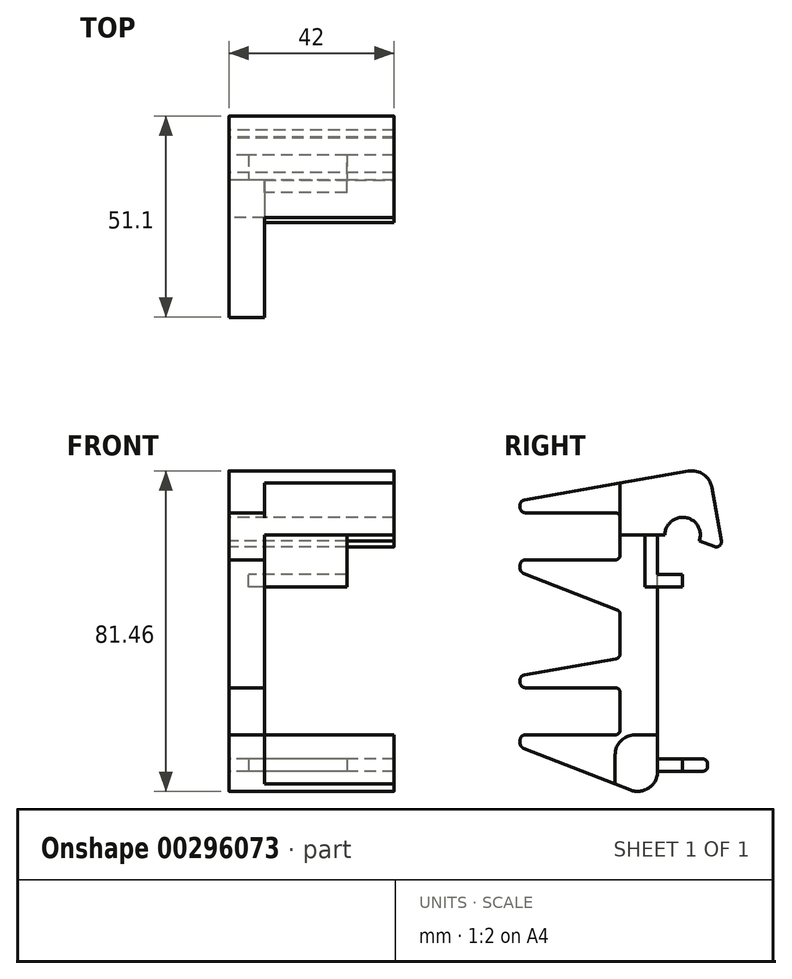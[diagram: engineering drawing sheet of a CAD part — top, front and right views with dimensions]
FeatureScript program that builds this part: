
annotation { "Feature Type Name" : "Feature", "Feature Type Description" : "" }
export const myFeature = defineFeature(function(context is Context, id is Id, definition is map)
    precondition{}
    {
        {
            var Q0;
            Q0=qCreatedBy(makeId("Right.planeOp"),FACE);
            var sketch = newSketch(context, id + "F0", { "sketchPlane" : qUnion([Q0])});
            skLineSegment(sketch, "E0.right", {"start": v(0, 67.5) * mm, "end": v(0, 0) * mm});
            skCircle(sketch, "E1", {"center": v(6.35, 67.5) * mm, "radius": 4.5 * mm});
            skLineSegment(sketch, "E2", {"start": v(1.85, 67.5) * mm, "end": v(0, 67.5) * mm});
            skLineSegment(sketch, "E3", {"start": v(16.55, 63.8) * mm, "end": v(10.58, 65.96) * mm});
            skLineSegment(sketch, "E4", {"start": v(-34.93, 58.1) * mm, "end": v(-34.93, 61.15) * mm});
            skLineSegment(sketch, "E5", {"start": v(-34.92, 61.15) * mm, "end": v(-9.52, 61.15) * mm});
            skLineSegment(sketch, "E6", {"start": v(-9.53, 61.15) * mm, "end": v(-9.53, 73.15) * mm});
            skLineSegment(sketch, "E7", {"start": v(-9.52, 73.15) * mm, "end": v(-34.92, 73.15) * mm});
            skLineSegment(sketch, "E8", {"start": v(-34.93, 73.15) * mm, "end": v(-34.93, 76.2) * mm});
            skLineSegment(sketch, "E9", {"start": v(-34.93, 31.75) * mm, "end": v(-34.93, 28.7) * mm});
            skLineSegment(sketch, "E10", {"start": v(-34.93, 28.7) * mm, "end": v(-9.52, 28.7) * mm});
            skLineSegment(sketch, "E11", {"start": v(-9.52, 28.7) * mm, "end": v(-9.52, 16.7) * mm});
            skLineSegment(sketch, "E12", {"start": v(-9.52, 16.7) * mm, "end": v(-34.92, 16.7) * mm});
            skLineSegment(sketch, "E13", {"start": v(-34.93, 16.7) * mm, "end": v(-34.93, 13.65) * mm});
            skLineSegment(sketch, "E14", {"start": v(-34.92, 13.65) * mm, "end": v(0, 0) * mm});
            skLineSegment(sketch, "E15", {"start": v(-34.92, 58.1) * mm, "end": v(-9.52, 48.17) * mm});
            skLineSegment(sketch, "E16", {"start": v(-9.53, 48.17) * mm, "end": v(-9.53, 36.23) * mm});
            skLineSegment(sketch, "E17", {"start": v(-34.93, 76.2) * mm, "end": v(12.87, 84.63) * mm});
            skLineSegment(sketch, "E18", {"start": v(-34.93, 31.75) * mm, "end": v(-9.52, 36.23) * mm});
            skLineSegment(sketch, "E19", {"start": v(12.87, 84.63) * mm, "end": v(16.55, 63.8) * mm});
            skSolve(sketch);
        }
        {
            var Q0;
            Q0=makeQuery(id+"F0.imprint","IMPRINT",FACE,{"disambiguationData":[TD([[makeQuery(id+"F0.imprint","IMPRINT",EDGE,{"derivedFrom":sQuery(id+"F0.wireOp",EDGE,"E0.right")}),-1.0]])]});
            extrude(context, id + "F1", {"entities" : qUnion([Q0]), "depth" : 42 * mm});
        }
        {
            var Q0;
            Q0=makeQuery(id+"F1.opExtrude","SWEPT_EDGE",EDGE,{"disambiguationData":[OSD([sQuery(id+"F0.wireOp",EDGE,"E17"),sQuery(id+"F0.wireOp",EDGE,"E19")])]});
            var Q1;
            Q1=makeQuery(id+"F1.opExtrude","SWEPT_EDGE",EDGE,{"disambiguationData":[OSD([sQuery(id+"F0.wireOp",EDGE,"E0.right"),sQuery(id+"F0.wireOp",EDGE,"E14")])]});
            fillet(context, id + "F2", {"entities" : qUnion([Q0, Q1]), "radius" : 5.08 * mm, "tangentPropagation" : true, "allowEdgeOverflow" : false});
        }
        {
            var Q0;
            Q0=makeQuery(id+"F1.opExtrude","SWEPT_EDGE",EDGE,{"disambiguationData":[OSD([sQuery(id+"F0.wireOp",EDGE,"E3"),sQuery(id+"F0.wireOp",EDGE,"E19")])]});
            var Q1;
            Q1=makeQuery(id+"F1.opExtrude","SWEPT_EDGE",EDGE,{"disambiguationData":[OSD([sQuery(id+"F0.wireOp",EDGE,"E10"),sQuery(id+"F0.wireOp",EDGE,"E11")])]});
            var Q2;
            Q2=makeQuery(id+"F1.opExtrude","SWEPT_EDGE",EDGE,{"disambiguationData":[OSD([sQuery(id+"F0.wireOp",EDGE,"E15"),sQuery(id+"F0.wireOp",EDGE,"E16")])]});
            var Q3;
            Q3=makeQuery(id+"F1.opExtrude","SWEPT_EDGE",EDGE,{"disambiguationData":[OSD([sQuery(id+"F0.wireOp",EDGE,"E6"),sQuery(id+"F0.wireOp",EDGE,"E7")])]});
            var Q4;
            Q4=makeQuery(id+"F1.opExtrude","SWEPT_EDGE",EDGE,{"disambiguationData":[OSD([sQuery(id+"F0.wireOp",EDGE,"E5"),sQuery(id+"F0.wireOp",EDGE,"E6")])]});
            var Q5;
            Q5=makeQuery(id+"F1.opExtrude","SWEPT_EDGE",EDGE,{"disambiguationData":[OSD([sQuery(id+"F0.wireOp",EDGE,"E11"),sQuery(id+"F0.wireOp",EDGE,"E12")])]});
            var Q6;
            Q6=makeQuery(id+"F1.opExtrude","SWEPT_EDGE",EDGE,{"disambiguationData":[OSD([sQuery(id+"F0.wireOp",EDGE,"E12"),sQuery(id+"F0.wireOp",EDGE,"E13")])]});
            var Q7;
            Q7=makeQuery(id+"F1.opExtrude","SWEPT_EDGE",EDGE,{"disambiguationData":[OSD([sQuery(id+"F0.wireOp",EDGE,"E13"),sQuery(id+"F0.wireOp",EDGE,"E14")])]});
            var Q8;
            Q8=makeQuery(id+"F1.opExtrude","SWEPT_EDGE",EDGE,{"disambiguationData":[OSD([sQuery(id+"F0.wireOp",EDGE,"E9"),sQuery(id+"F0.wireOp",EDGE,"E10")])]});
            var Q9;
            Q9=makeQuery(id+"F1.opExtrude","SWEPT_EDGE",EDGE,{"disambiguationData":[OSD([sQuery(id+"F0.wireOp",EDGE,"E4"),sQuery(id+"F0.wireOp",EDGE,"E5")])]});
            var Q10;
            Q10=makeQuery(id+"F1.opExtrude","SWEPT_EDGE",EDGE,{"disambiguationData":[OSD([sQuery(id+"F0.wireOp",EDGE,"E4"),sQuery(id+"F0.wireOp",EDGE,"E15")])]});
            var Q11;
            Q11=makeQuery(id+"F1.opExtrude","SWEPT_EDGE",EDGE,{"disambiguationData":[OSD([sQuery(id+"F0.wireOp",EDGE,"E9"),sQuery(id+"F0.wireOp",EDGE,"E18")])]});
            var Q12;
            Q12=makeQuery(id+"F1.opExtrude","SWEPT_EDGE",EDGE,{"disambiguationData":[OSD([sQuery(id+"F0.wireOp",EDGE,"E7"),sQuery(id+"F0.wireOp",EDGE,"E8")])]});
            var Q13;
            Q13=makeQuery(id+"F1.opExtrude","SWEPT_EDGE",EDGE,{"disambiguationData":[OSD([sQuery(id+"F0.wireOp",EDGE,"E8"),sQuery(id+"F0.wireOp",EDGE,"E17")])]});
            var Q14;
            Q14=makeQuery(id+"F1.opExtrude","SWEPT_EDGE",EDGE,{"disambiguationData":[OSD([sQuery(id+"F0.wireOp",EDGE,"E16"),sQuery(id+"F0.wireOp",EDGE,"E18")])]});
            fillet(context, id + "F3", {"entities" : qUnion([Q0, Q1, Q2, Q3, Q4, Q5, Q6, Q7, Q8, Q9, Q10, Q11, Q12, Q13, Q14]), "radius" : 1.27 * mm, "tangentPropagation" : true, "allowEdgeOverflow" : false});
        }
        {
            var Q0;
            Q0=makeQuery(id+"F1.opExtrude","SWEPT_FACE",FACE,{"disambiguationData":[OSD([sQuery(id+"F0.wireOp",EDGE,"E0.right")])]});
            var sketch = newSketch(context, id + "F4", { "sketchPlane" : qUnion([Q0])});
            skLineSegment(sketch, "E20.bottom", {"start": v(-30, 10.62) * mm, "end": v(-5, 10.62) * mm});
            skLineSegment(sketch, "E20.top", {"start": v(-30, 7.44) * mm, "end": v(-5, 7.44) * mm});
            skLineSegment(sketch, "E20.left", {"start": v(-30, 10.62) * mm, "end": v(-30, 7.44) * mm});
            skLineSegment(sketch, "E20.right", {"start": v(-5, 10.62) * mm, "end": v(-5, 7.44) * mm});
            skSolve(sketch);
        }
        {
            var Q0;
            Q0 = qSketchRegion(id + "F4", true);
            extrude(context, id + "F5", {"entities" : qUnion([Q0]), "operationType" : NewBodyOperationType.ADD, "depth" : 12.7 * mm});
        }
        {
            var Q0;
            Q0=makeQuery(id+"F1.opExtrude","CAP_FACE",FACE,{"disambiguationData":[OSD([sQuery(id+"F0.wireOp",EDGE,"E0.right"),sQuery(id+"F0.wireOp",EDGE,"E1"),sQuery(id+"F0.wireOp",EDGE,"E2"),sQuery(id+"F0.wireOp",EDGE,"E3"),sQuery(id+"F0.wireOp",EDGE,"E4"),sQuery(id+"F0.wireOp",EDGE,"E5"),sQuery(id+"F0.wireOp",EDGE,"E6"),sQuery(id+"F0.wireOp",EDGE,"E7"),sQuery(id+"F0.wireOp",EDGE,"E8"),sQuery(id+"F0.wireOp",EDGE,"E9"),sQuery(id+"F0.wireOp",EDGE,"E10"),sQuery(id+"F0.wireOp",EDGE,"E11"),sQuery(id+"F0.wireOp",EDGE,"E12"),sQuery(id+"F0.wireOp",EDGE,"E13"),sQuery(id+"F0.wireOp",EDGE,"E14"),sQuery(id+"F0.wireOp",EDGE,"E15"),sQuery(id+"F0.wireOp",EDGE,"E16"),sQuery(id+"F0.wireOp",EDGE,"E17"),sQuery(id+"F0.wireOp",EDGE,"E18"),sQuery(id+"F0.wireOp",EDGE,"E19")])],"isStart":false});
            var sketch = newSketch(context, id + "F6", { "sketchPlane" : qUnion([Q0])});
            skLineSegment(sketch, "E21.left", {"start": v(0, 67.5) * mm, "end": v(0, 16.7) * mm});
            skLineSegment(sketch, "E21.right", {"start": v(-34.93, 80.68) * mm, "end": v(-34.93, 4.22) * mm});
            skLineSegment(sketch, "E22", {"start": v(0, 67.5) * mm, "end": v(-9.53, 67.5) * mm});
            skLineSegment(sketch, "E23", {"start": v(-9.53, 67.5) * mm, "end": v(-9.53, 80.68) * mm});
            skLineSegment(sketch, "E24", {"start": v(-34.93, 80.68) * mm, "end": v(-9.53, 80.68) * mm});
            skLineSegment(sketch, "E25", {"start": v(0, 16.7) * mm, "end": v(-10.8, 16.7) * mm});
            skLineSegment(sketch, "E26", {"start": v(-10.8, 16.7) * mm, "end": v(-10.8, 4.22) * mm});
            skLineSegment(sketch, "E27", {"start": v(-10.8, 4.22) * mm, "end": v(-34.93, 4.22) * mm});
            skSolve(sketch);
        }
        {
            var Q0;
            Q0 = qSketchRegion(id + "F6", true);
            extrude(context, id + "F7", {"entities" : qUnion([Q0]), "operationType" : NewBodyOperationType.REMOVE, "oppositeDirection" : true, "depth" : 33 * mm});
        }
        {
            var Q0;
            Q0=makeQuery(id+"F7.boolean.opBoolean","COPY",EDGE,{"derivedFrom":makeQuery(id+"F7.opExtrude","SWEPT_EDGE",EDGE,{"disambiguationData":[OSD([sQuery(id+"F0.wireOp",EDGE,"E6"),sQuery(id+"F6.wireOp",EDGE,"E22"),sQuery(id+"F6.wireOp",EDGE,"E23")])]})});
            var Q1;
            Q1=makeQuery(id+"F7.boolean.opBoolean","COPY",EDGE,{"derivedFrom":makeQuery(id+"F7.opExtrude","SWEPT_EDGE",EDGE,{"disambiguationData":[OSD([sQuery(id+"F0.wireOp",EDGE,"E17"),sQuery(id+"F6.wireOp",EDGE,"E23"),sQuery(id+"F6.wireOp",EDGE,"E24")])]})});
            var Q2;
            Q2=makeQuery(id+"F7.boolean.opBoolean","COPY",EDGE,{"derivedFrom":makeQuery(id+"F7.opExtrude","SWEPT_EDGE",EDGE,{"disambiguationData":[OSD([sQuery(id+"F0.wireOp",EDGE,"E0.right"),sQuery(id+"F0.wireOp",EDGE,"E1"),sQuery(id+"F0.wireOp",EDGE,"E2"),sQuery(id+"F0.wireOp",EDGE,"E3"),sQuery(id+"F0.wireOp",EDGE,"E4"),sQuery(id+"F0.wireOp",EDGE,"E5"),sQuery(id+"F0.wireOp",EDGE,"E6"),sQuery(id+"F0.wireOp",EDGE,"E7"),sQuery(id+"F0.wireOp",EDGE,"E8"),sQuery(id+"F0.wireOp",EDGE,"E9"),sQuery(id+"F0.wireOp",EDGE,"E10"),sQuery(id+"F0.wireOp",EDGE,"E11"),sQuery(id+"F0.wireOp",EDGE,"E12"),sQuery(id+"F0.wireOp",EDGE,"E13"),sQuery(id+"F0.wireOp",EDGE,"E14"),sQuery(id+"F0.wireOp",EDGE,"E15"),sQuery(id+"F0.wireOp",EDGE,"E16"),sQuery(id+"F0.wireOp",EDGE,"E17"),sQuery(id+"F0.wireOp",EDGE,"E18"),sQuery(id+"F0.wireOp",EDGE,"E19"),sQuery(id+"F6.wireOp",EDGE,"E25"),sQuery(id+"F6.wireOp",EDGE,"E26")])]})});
            var Q3;
            Q3=makeQuery(id+"F7.boolean.opBoolean","COPY",EDGE,{"derivedFrom":makeQuery(id+"F7.opExtrude","SWEPT_EDGE",EDGE,{"disambiguationData":[OSD([sQuery(id+"F0.wireOp",EDGE,"E14"),sQuery(id+"F6.wireOp",EDGE,"E26"),sQuery(id+"F6.wireOp",EDGE,"E27")])]})});
            var Q4;
            Q4=makeQuery(id+"F7.boolean.opBoolean","COPY",EDGE,{"derivedFrom":makeQuery(id+"F7.opExtrude","SWEPT_EDGE",EDGE,{"disambiguationData":[OSD([sQuery(id+"F0.wireOp",EDGE,"E0.right"),sQuery(id+"F6.wireOp",EDGE,"E21.left"),sQuery(id+"F6.wireOp",EDGE,"E25")])]})});
            fillet(context, id + "F8", {"entities" : qUnion([Q0, Q1, Q2, Q3, Q4]), "radius" : 5.08 * mm, "tangentPropagation" : true, "allowEdgeOverflow" : false});
        }
        {
            var Q0;
            Q0=makeQuery(id+"F5.opExtrude","SWEPT_FACE",FACE,{"disambiguationData":[OSD([sQuery(id+"F4.wireOp",EDGE,"E20.left")])]});
            var sketch = newSketch(context, id + "F9", { "sketchPlane" : qUnion([Q0])});
            skLineSegment(sketch, "E28", {"start": v(6.35, 10.62) * mm, "end": v(6.35, 7.44) * mm});
            skSolve(sketch);
        }
        {
            var Q0;
            {var subQ6=sQuery(id+"F9.wireOp",EDGE,"E28");Q0=makeQuery(id+"F9.imprint","IMPRINT",FACE,{"disambiguationData":[TD([[makeQuery(id+"F9.imprint","IMPRINT",EDGE,{"derivedFrom":subQ6}),1.0]])]});}
            var Q1;
            {var subQ0=sQuery(id+"F0.wireOp",EDGE,"E14");var subQ1=sQuery(id+"F0.wireOp",EDGE,"E0.right");Q1=makeQuery(id+"F7.boolean.opBoolean","SPLIT",FACE,{"disambiguationData":[TD([makeQuery(id+"F1.opExtrude","SWEPT_FACE",FACE,{"disambiguationData":[OSD([subQ1])]})])],"derivedFrom":makeQuery(id+"F1.opExtrude","CAP_FACE",FACE,{"disambiguationData":[OSD([subQ1,sQuery(id+"F0.wireOp",EDGE,"E1"),sQuery(id+"F0.wireOp",EDGE,"E2"),sQuery(id+"F0.wireOp",EDGE,"E3"),sQuery(id+"F0.wireOp",EDGE,"E4"),sQuery(id+"F0.wireOp",EDGE,"E5"),sQuery(id+"F0.wireOp",EDGE,"E6"),sQuery(id+"F0.wireOp",EDGE,"E7"),sQuery(id+"F0.wireOp",EDGE,"E8"),sQuery(id+"F0.wireOp",EDGE,"E9"),sQuery(id+"F0.wireOp",EDGE,"E10"),sQuery(id+"F0.wireOp",EDGE,"E11"),sQuery(id+"F0.wireOp",EDGE,"E12"),sQuery(id+"F0.wireOp",EDGE,"E13"),subQ0,sQuery(id+"F0.wireOp",EDGE,"E15"),sQuery(id+"F0.wireOp",EDGE,"E16"),sQuery(id+"F0.wireOp",EDGE,"E17"),sQuery(id+"F0.wireOp",EDGE,"E18"),sQuery(id+"F0.wireOp",EDGE,"E19")])],"isStart":false})});}
            var Q2;
            Q2=makeQuery(id+"F1.opExtrude","CAP_FACE",FACE,{"disambiguationData":[OSD([sQuery(id+"F0.wireOp",EDGE,"E0.right"),sQuery(id+"F0.wireOp",EDGE,"E1"),sQuery(id+"F0.wireOp",EDGE,"E2"),sQuery(id+"F0.wireOp",EDGE,"E3"),sQuery(id+"F0.wireOp",EDGE,"E4"),sQuery(id+"F0.wireOp",EDGE,"E5"),sQuery(id+"F0.wireOp",EDGE,"E6"),sQuery(id+"F0.wireOp",EDGE,"E7"),sQuery(id+"F0.wireOp",EDGE,"E8"),sQuery(id+"F0.wireOp",EDGE,"E9"),sQuery(id+"F0.wireOp",EDGE,"E10"),sQuery(id+"F0.wireOp",EDGE,"E11"),sQuery(id+"F0.wireOp",EDGE,"E12"),sQuery(id+"F0.wireOp",EDGE,"E13"),sQuery(id+"F0.wireOp",EDGE,"E14"),sQuery(id+"F0.wireOp",EDGE,"E15"),sQuery(id+"F0.wireOp",EDGE,"E16"),sQuery(id+"F0.wireOp",EDGE,"E17"),sQuery(id+"F0.wireOp",EDGE,"E18"),sQuery(id+"F0.wireOp",EDGE,"E19")])],"isStart":true});
            extrude(context, id + "F10", {"entities" : qUnion([Q0]), "operationType" : NewBodyOperationType.ADD, "endBound" : BoundingType.UP_TO_SURFACE, "endBoundEntityFace" : qUnion([Q1]), "depth" : 25 * mm, "hasSecondDirection" : true, "secondDirectionBound" : SecondDirectionBoundingType.UP_TO_SURFACE, "secondDirectionOppositeDirection" : true, "secondDirectionBoundEntityFace" : qUnion([Q2]), "secondDirectionDepth" : 25 * mm});
        }
        {
            var Q0;
            {var subQ11=sQuery(id+"F6.wireOp",EDGE,"E26");var subQ12=sQuery(id+"F6.wireOp",EDGE,"E25");var subQ13=sQuery(id+"F6.wireOp",EDGE,"E23");var subQ14=sQuery(id+"F6.wireOp",EDGE,"E22");var subQ15=makeQuery(id+"F7.opExtrude","CAP_FACE",FACE,{"disambiguationData":[OSD([sQuery(id+"F6.wireOp",EDGE,"E21.left"),sQuery(id+"F6.wireOp",EDGE,"E21.right"),subQ14,subQ13,sQuery(id+"F6.wireOp",EDGE,"E24"),subQ12,subQ11,sQuery(id+"F6.wireOp",EDGE,"E27")])],"isStart":false});var subQ20=sQuery(id+"F0.wireOp",EDGE,"E13");Q0=makeQuery(id+"F8.opFillet","MERGE",FACE,{"derivedFrom":[makeQuery(id+"F7.boolean.opBoolean","COPY",FACE,{"disambiguationData":[TD([makeQuery(id+"F1.opExtrude","SWEPT_FACE",FACE,{"disambiguationData":[OSD([subQ20])]})])],"derivedFrom":subQ15}),makeQuery(id+"F7.boolean.opBoolean","COPY",FACE,{"disambiguationData":[TD([makeQuery(id+"F1.opExtrude","SWEPT_FACE",FACE,{"disambiguationData":[OSD([sQuery(id+"F0.wireOp",EDGE,"E0.right")])]})])],"derivedFrom":subQ15})]});}
            var sketch = newSketch(context, id + "F11", { "sketchPlane" : qUnion([Q0])});
            skLineSegment(sketch, "E29.bottom", {"start": v(0, 67.5) * mm, "end": v(-3.18, 67.5) * mm});
            skLineSegment(sketch, "E29.right", {"start": v(-3.18, 67.5) * mm, "end": v(-3.18, 54.33) * mm});
            skLineSegment(sketch, "E30", {"start": v(0, 67.5) * mm, "end": v(0, 57.5) * mm});
            skLineSegment(sketch, "E31", {"start": v(0, 57.5) * mm, "end": v(6.35, 57.5) * mm});
            skLineSegment(sketch, "E32", {"start": v(6.35, 57.5) * mm, "end": v(6.35, 54.33) * mm});
            skLineSegment(sketch, "E33", {"start": v(6.35, 54.33) * mm, "end": v(-3.18, 54.33) * mm});
            skSolve(sketch);
        }
        {
            var Q0;
            Q0 = qSketchRegion(id + "F11", true);
            var Q1;
            Q1=makeQuery(id+"F5.opExtrude","SWEPT_FACE",FACE,{"disambiguationData":[OSD([sQuery(id+"F4.wireOp",EDGE,"E20.left")])]});
            var Q2;
            Q2=makeQuery(id+"F5.opExtrude","SWEPT_FACE",FACE,{"disambiguationData":[OSD([sQuery(id+"F4.wireOp",EDGE,"E20.right")])]});
            extrude(context, id + "F12", {"entities" : qUnion([Q0]), "operationType" : NewBodyOperationType.ADD, "endBound" : BoundingType.UP_TO_SURFACE, "endBoundEntityFace" : qUnion([Q1]), "depth" : 25 * mm, "hasSecondDirection" : true, "secondDirectionBound" : SecondDirectionBoundingType.UP_TO_SURFACE, "secondDirectionOppositeDirection" : true, "secondDirectionBoundEntityFace" : qUnion([Q2]), "secondDirectionDepth" : 25 * mm});
        }
        {
            var Q0;
            Q0=makeQuery(id+"F5.opExtrude","CAP_EDGE",EDGE,{"disambiguationData":[OSD([sQuery(id+"F4.wireOp",EDGE,"E20.bottom")])],"isStart":false});
            var Q1;
            Q1=makeQuery(id+"F5.opExtrude","CAP_EDGE",EDGE,{"disambiguationData":[OSD([sQuery(id+"F4.wireOp",EDGE,"E20.top")])],"isStart":false});
            var Q2;
            Q2=makeQuery(id+"F12.opExtrude","TWEAK_EDGE",EDGE,{"derivedFrom":[makeQuery(id+"F11.imprint","IMPRINT",EDGE,{"derivedFrom":sQuery(id+"F11.wireOp",EDGE,"E31")}),makeQuery(id+"F11.imprint","IMPRINT",EDGE,{"derivedFrom":sQuery(id+"F11.wireOp",EDGE,"E32")})]});
            var Q3;
            {var subQ0=sQuery(id+"F11.wireOp",EDGE,"E33");var subQ2=sQuery(id+"F11.wireOp",EDGE,"E32");Q3=makeQuery(id+"F12.opExtrude","TWEAK_EDGE",EDGE,{"derivedFrom":[makeQuery(id+"F11.imprint","IMPRINT",EDGE,{"derivedFrom":subQ2}),makeQuery(id+"F11.imprint","IMPRINT",EDGE,{"disambiguationData":[TD([[makeQuery(id+"F11.imprint","INTERSECT",VERTEX,{"derivedFrom":[subQ2,subQ0]}),-1.0]])],"derivedFrom":subQ0}),makeQuery(id+"F11.imprint","IMPRINT",EDGE,{"disambiguationData":[TD([[makeQuery(id+"F11.imprint","INTERSECT",VERTEX,{"derivedFrom":[sQuery(id+"F11.wireOp",EDGE,"E29.right"),subQ0]}),1.0]])],"derivedFrom":subQ0})]});}
            var Q4;
            {var subQ0=sQuery(id+"F11.wireOp",EDGE,"E33");var subQ1=sQuery(id+"F11.wireOp",EDGE,"E29.right");Q4=makeQuery(id+"F12.opExtrude","TWEAK_EDGE",EDGE,{"derivedFrom":[makeQuery(id+"F11.imprint","IMPRINT",EDGE,{"derivedFrom":subQ1}),makeQuery(id+"F11.imprint","IMPRINT",EDGE,{"disambiguationData":[TD([[makeQuery(id+"F11.imprint","INTERSECT",VERTEX,{"derivedFrom":[sQuery(id+"F11.wireOp",EDGE,"E32"),subQ0]}),-1.0]])],"derivedFrom":subQ0}),makeQuery(id+"F11.imprint","IMPRINT",EDGE,{"disambiguationData":[TD([[makeQuery(id+"F11.imprint","INTERSECT",VERTEX,{"derivedFrom":[subQ1,subQ0]}),1.0]])],"derivedFrom":subQ0})]});}
            fillet(context, id + "F13", {"entities" : qUnion([Q0, Q1, Q2, Q3, Q4]), "radius" : 1.27 * mm, "tangentPropagation" : true, "allowEdgeOverflow" : false});
        }
    });
